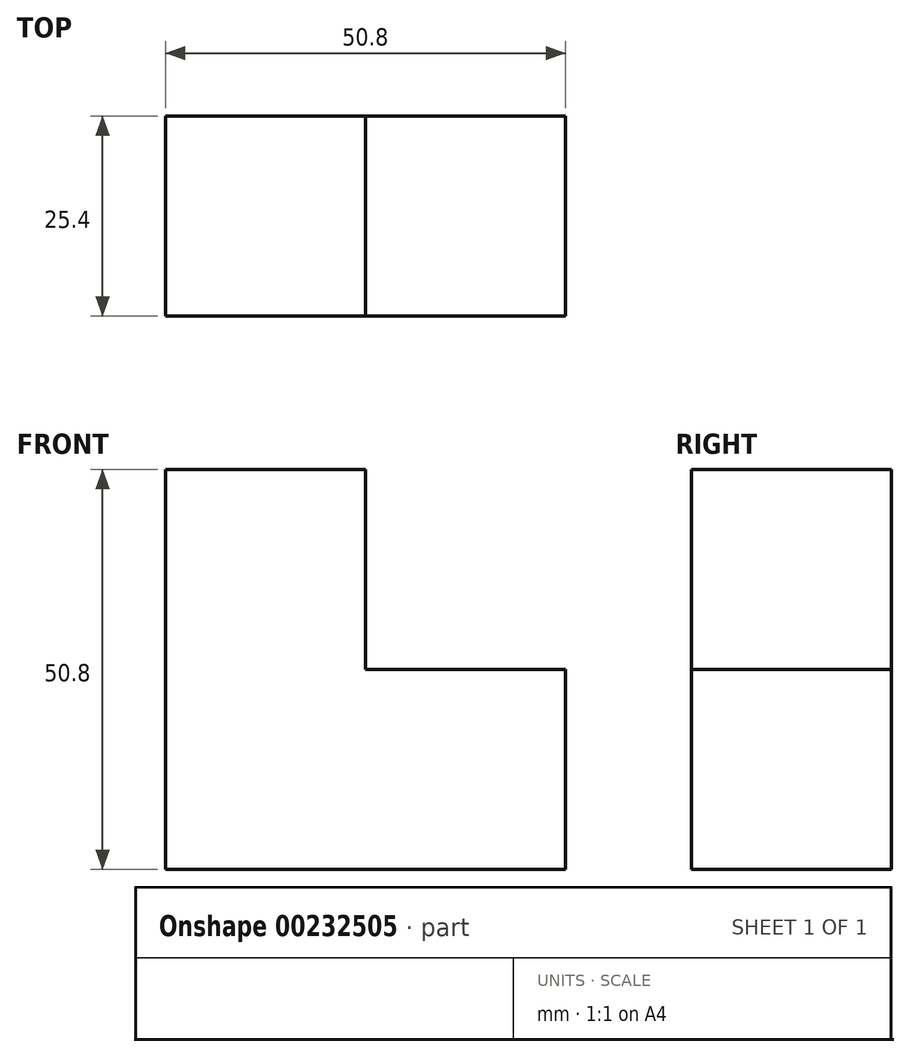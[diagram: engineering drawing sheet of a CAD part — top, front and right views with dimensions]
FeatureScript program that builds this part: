
annotation { "Feature Type Name" : "Feature", "Feature Type Description" : "" }
export const myFeature = defineFeature(function(context is Context, id is Id, definition is map)
    precondition{}
    {
        {
            var Q0;
            Q0=qCreatedBy(makeId("Front.planeOp"),FACE);
            var sketch = newSketch(context, id + "F0", { "sketchPlane" : qUnion([Q0])});
            skLineSegment(sketch, "E0.bottom", {"start": v(0, 0) * mm, "end": v(25.4, 0) * mm});
            skLineSegment(sketch, "E0.top", {"start": v(0, 50.8) * mm, "end": v(25.4, 50.8) * mm});
            skLineSegment(sketch, "E0.left", {"start": v(0, 0) * mm, "end": v(0, 50.8) * mm});
            skLineSegment(sketch, "E0.right", {"start": v(25.4, 0) * mm, "end": v(25.4, 50.8) * mm});
            skLineSegment(sketch, "E1.bottom", {"start": v(0, 25.4) * mm, "end": v(50.8, 25.4) * mm});
            skLineSegment(sketch, "E1.top", {"start": v(0, 0) * mm, "end": v(50.8, 0) * mm});
            skLineSegment(sketch, "E1.left", {"start": v(0, 25.4) * mm, "end": v(0, 0) * mm});
            skLineSegment(sketch, "E1.right", {"start": v(50.8, 25.4) * mm, "end": v(50.8, 0) * mm});
            skSolve(sketch);
        }
        {
            var Q0;
            Q0 = qSketchRegion(id + "F0", true);
            extrude(context, id + "F1", {"entities" : qUnion([Q0]), "depth" : 25.4 * mm});
        }
    });
